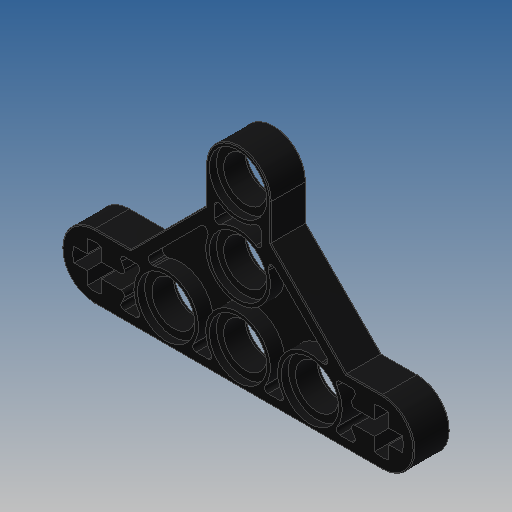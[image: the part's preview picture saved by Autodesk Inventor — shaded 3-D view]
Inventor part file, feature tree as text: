
AUTODESK INVENTOR PART (.ipt)
format: ipt  version: 2022.2 (Build 262287000, 287)  size: 414,720 bytes
history: native  units: in
note: dims shown in document units (in); Inventor stores cm internally (conversion verified against a paired STEP export)
features: extrude x3, sketch x2, mirror x1, fillet x1
ambient origin geometry x8: Origin, YZ Plane, XZ Plane, XY Plane, X Axis, Y Axis, Z Axis, Center Point
bodies: Solid1 (feature_tree)
feature tree (7):
  sketch  "Sketch1"  dims[d0=0.315in d1=0.189in]
  extrude  "Extrusion1"  Depth=0.315in
  extrude  "Extrusion2"  Depth=0.2835in
  extrude  "Extrusion3"  Depth=0.0394in
  mirror  "Mirror1"
  fillet  "Fillet1"  Radius=0.0394in
  sketch  "Sketch2"  dims[d2=0.189in d3=0.2835in d5=0.0394in d6=0.0394in d7=0.063in d8=0.063in d9=0.1575in d10=0.0in d11=0.0315in d12=0.0in d13=0.252in d14=0.0315in d15=0.0in d16=0.0039in d17=0.1575in d18=0.0445in d20=15.0deg d21=0.0157in]
